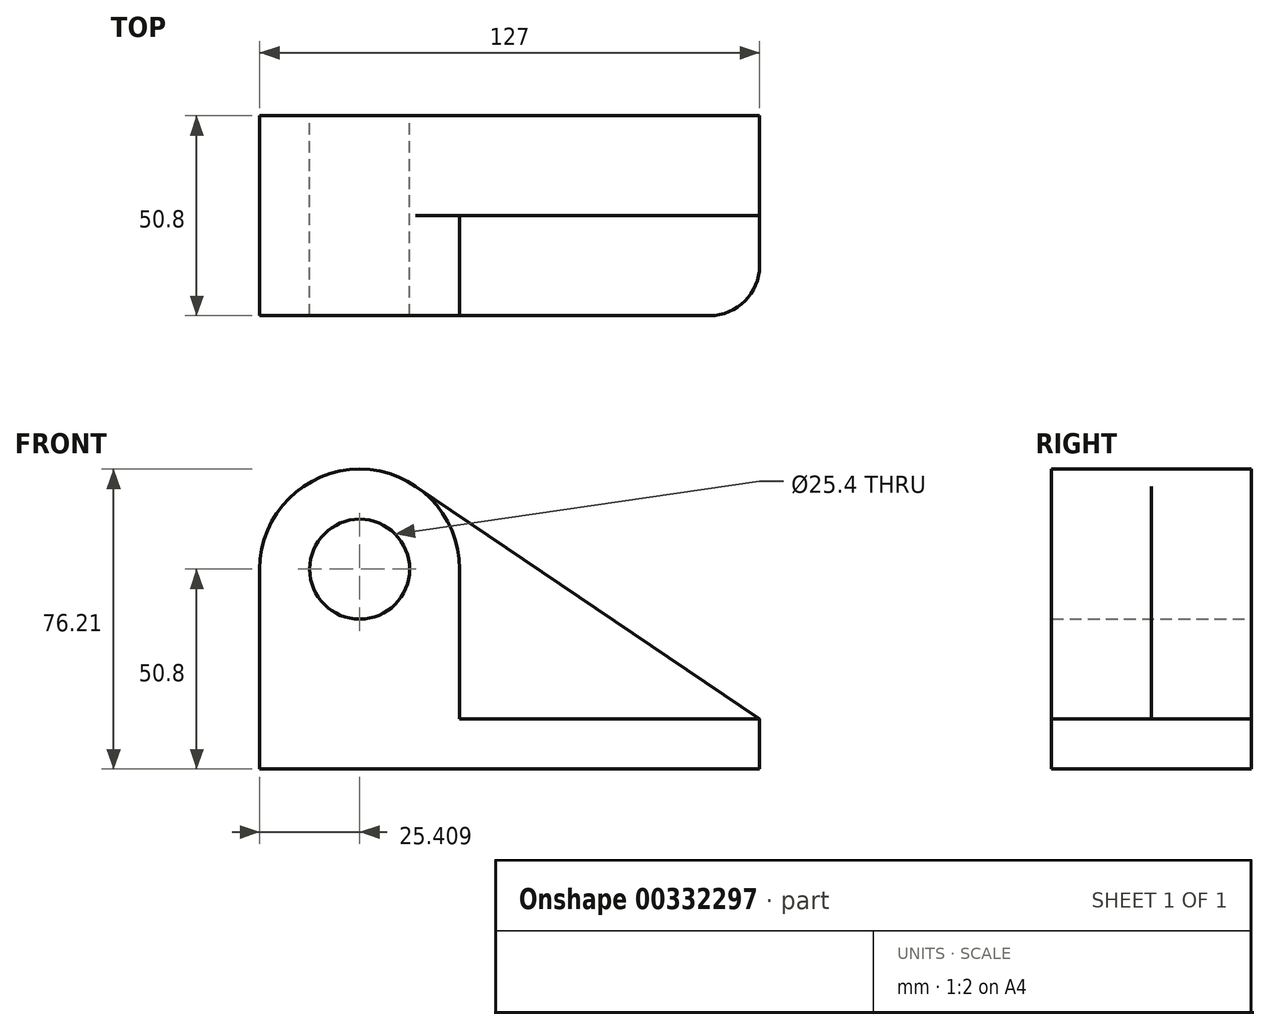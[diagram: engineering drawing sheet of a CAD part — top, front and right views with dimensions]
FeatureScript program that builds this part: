
annotation { "Feature Type Name" : "Feature", "Feature Type Description" : "" }
export const myFeature = defineFeature(function(context is Context, id is Id, definition is map)
    precondition{}
    {
        {
            var Q0;
            Q0=qCreatedBy(makeId("Front.planeOp"),FACE);
            var sketch = newSketch(context, id + "F0", { "sketchPlane" : qUnion([Q0])});
            skCircle(sketch, "E0", {"center": v(-40.48, 50.8) * mm, "radius": 12.7 * mm});
            skArc(sketch, "E1", {"start": v(-26.24, 71.84) * mm, "mid": v(-52.39, 73.24) * mm, "end": v(-65.89, 50.8) * mm});
            skLineSegment(sketch, "E2", {"start": v(-65.89, 50.8) * mm, "end": v(-65.89, 0) * mm});
            skLineSegment(sketch, "E3", {"start": v(-65.89, 0) * mm, "end": v(61.11, 0) * mm});
            skLineSegment(sketch, "E4", {"start": v(61.11, 0) * mm, "end": v(61.11, 12.7) * mm});
            skLineSegment(sketch, "E5", {"start": v(61.11, 12.7) * mm, "end": v(-26.24, 71.84) * mm});
            skSolve(sketch);
        }
        {
            var Q0;
            Q0 = qSketchRegion(id + "F0", true);
            extrude(context, id + "F1", {"entities" : qUnion([Q0]), "depth" : 25.4 * mm});
        }
        {
            var Q0;
            Q0=makeQuery(id+"F1.opExtrude","CAP_FACE",FACE,{"disambiguationData":[OSD([sQuery(id+"F0.wireOp",EDGE,"E0"),sQuery(id+"F0.wireOp",EDGE,"E1"),sQuery(id+"F0.wireOp",EDGE,"E2"),sQuery(id+"F0.wireOp",EDGE,"E3"),sQuery(id+"F0.wireOp",EDGE,"E4"),sQuery(id+"F0.wireOp",EDGE,"E5")])],"isStart":false});
            var sketch = newSketch(context, id + "F2", { "sketchPlane" : qUnion([Q0])});
            skCircle(sketch, "E6", {"center": v(-40.48, 50.8) * mm, "radius": 12.7 * mm});
            skLineSegment(sketch, "E7.bottom", {"start": v(61.11, 12.7) * mm, "end": v(-15.07, 12.7) * mm});
            skLineSegment(sketch, "E7.top", {"start": v(61.11, 0) * mm, "end": v(-65.89, 0) * mm});
            skLineSegment(sketch, "E7.left", {"start": v(61.11, 12.7) * mm, "end": v(61.11, 0) * mm});
            skLineSegment(sketch, "E7.right", {"start": v(-65.89, 12.7) * mm, "end": v(-65.89, 0) * mm});
            skLineSegment(sketch, "E8", {"start": v(-65.89, 50.8) * mm, "end": v(-65.89, 12.7) * mm});
            skLineSegment(sketch, "E9", {"start": v(-15.07, 50.8) * mm, "end": v(-15.07, 12.7) * mm});
            skArc(sketch, "E10", {"start": v(-15.07, 50.8) * mm, "mid": v(-40.48, 76.2) * mm, "end": v(-65.89, 50.8) * mm});
            skSolve(sketch);
        }
        {
            var Q0;
            Q0=makeQuery(id+"F2.imprint","IMPRINT",FACE,{"disambiguationData":[TD([[makeQuery(id+"F2.imprint","IMPRINT",EDGE,{"derivedFrom":sQuery(id+"F2.wireOp",EDGE,"E6")}),-1.0]])]});
            extrude(context, id + "F3", {"entities" : qUnion([Q0]), "operationType" : NewBodyOperationType.ADD, "depth" : 25.4 * mm});
        }
        {
            var Q0;
            Q0=makeQuery(id+"F3.opExtrude","CAP_EDGE",EDGE,{"disambiguationData":[OSD([sQuery(id+"F2.wireOp",EDGE,"E7.left")])],"isStart":false});
            fillet(context, id + "F4", {"entities" : qUnion([Q0]), "radius" : 12.7 * mm, "tangentPropagation" : true, "allowEdgeOverflow" : false});
        }
    });
